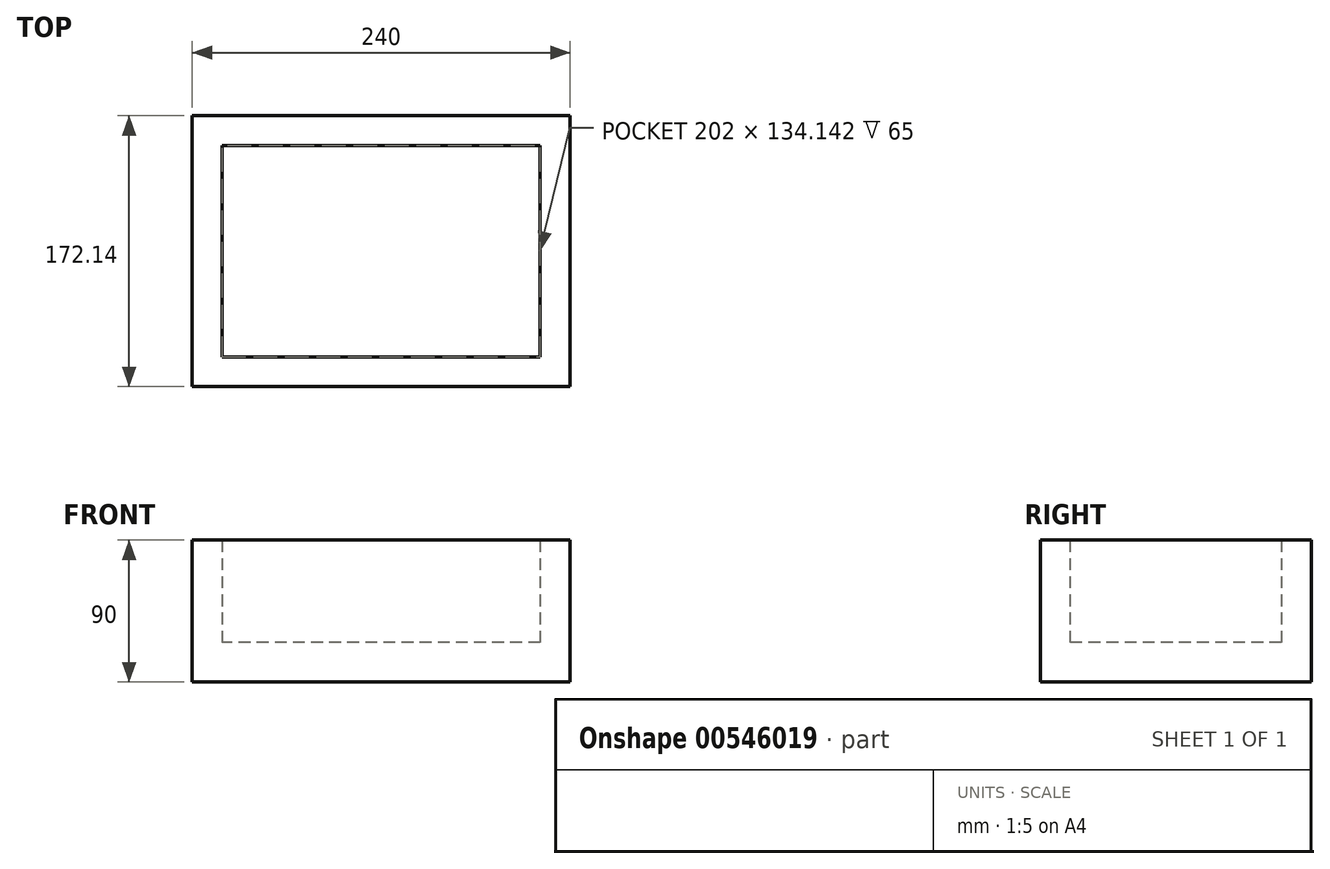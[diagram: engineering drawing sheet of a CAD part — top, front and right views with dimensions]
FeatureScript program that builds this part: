
annotation { "Feature Type Name" : "Feature", "Feature Type Description" : "" }
export const myFeature = defineFeature(function(context is Context, id is Id, definition is map)
    precondition{}
    {
        {
            var Q0;
            Q0=qCreatedBy(makeId("Top.planeOp"),FACE);
            var sketch = newSketch(context, id + "F0", { "sketchPlane" : qUnion([Q0])});
            skLineSegment(sketch, "E0.bottom", {"start": v(-120, 86.07) * mm, "end": v(120, 86.07) * mm});
            skLineSegment(sketch, "E0.top", {"start": v(-120, -86.07) * mm, "end": v(120, -86.07) * mm});
            skLineSegment(sketch, "E0.left", {"start": v(-120, 86.07) * mm, "end": v(-120, -86.07) * mm});
            skLineSegment(sketch, "E0.right", {"start": v(120, 86.07) * mm, "end": v(120, -86.07) * mm});
            skPoint(sketch, "E0.middle", {"position": v(0, 0) * mm});
            skSolve(sketch);
        }
        {
            var Q0;
            Q0 = qSketchRegion(id + "F0", true);
            extrude(context, id + "F1", {"entities" : qUnion([Q0]), "depth" : 25 * mm, "offsetDistance" : 25 * mm});
        }
        {
            var Q0;
            Q0=makeQuery(id+"F1.opExtrude","CAP_FACE",FACE,{"disambiguationData":[OSD([sQuery(id+"F0.wireOp",EDGE,"E0.bottom"),sQuery(id+"F0.wireOp",EDGE,"E0.top"),sQuery(id+"F0.wireOp",EDGE,"E0.left"),sQuery(id+"F0.wireOp",EDGE,"E0.right")])],"isStart":false});
            var sketch = newSketch(context, id + "F2", { "sketchPlane" : qUnion([Q0])});
            skLineSegment(sketch, "E1.bottom", {"start": v(-120, -86.07) * mm, "end": v(120, -86.07) * mm});
            skLineSegment(sketch, "E1.top", {"start": v(-120, 86.07) * mm, "end": v(120, 86.07) * mm});
            skLineSegment(sketch, "E1.left", {"start": v(-120, -86.07) * mm, "end": v(-120, 86.07) * mm});
            skLineSegment(sketch, "E1.right", {"start": v(120, -86.07) * mm, "end": v(120, 86.07) * mm});
            skLineSegment(sketch, "E2.bottom", {"start": v(101, 67.07) * mm, "end": v(-101, 67.07) * mm});
            skLineSegment(sketch, "E2.top", {"start": v(101, -67.07) * mm, "end": v(-101, -67.07) * mm});
            skLineSegment(sketch, "E2.left", {"start": v(101, 67.07) * mm, "end": v(101, -67.07) * mm});
            skLineSegment(sketch, "E2.right", {"start": v(-101, 67.07) * mm, "end": v(-101, -67.07) * mm});
            skPoint(sketch, "E2.middle", {"position": v(0, 0) * mm});
            skSolve(sketch);
        }
        {
            var Q0;
            Q0=makeQuery(id+"F2.imprint","IMPRINT",FACE,{"disambiguationData":[TD([[makeQuery(id+"F2.imprint","IMPRINT",EDGE,{"derivedFrom":sQuery(id+"F2.wireOp",EDGE,"E1.bottom")}),1.0]])]});
            extrude(context, id + "F3", {"entities" : qUnion([Q0]), "operationType" : NewBodyOperationType.ADD, "depth" : 65 * mm, "offsetDistance" : 25 * mm});
        }
    });
